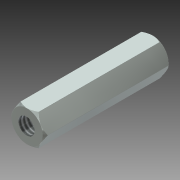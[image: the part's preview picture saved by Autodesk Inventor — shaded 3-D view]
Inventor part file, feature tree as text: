
AUTODESK INVENTOR PART (.ipt)
format: ipt  version: 2013 (Build 170138000, 138)  size: 134,144 bytes
history: native  units: mm (DEFAULTED — no unit token found)
features: sketch x4, plane x2, hole x2, extrude x1, revolve x1
ambient origin geometry x8: Origin, YZ Plane, XZ Plane, XY Plane, X Axis, Y Axis, Z Axis, Center Point
bodies: Solid1 (feature_tree)
feature tree (10):
  extrude  "Extrusion1"  Depth=25.4mm TaperAngle=0.0deg
  plane  "Work Plane1"
  revolve  "Revolution1"  [1 undecoded]
  hole  "Hole3"  [1 undecoded]
  hole  "Hole4"  [1 undecoded]
  plane  "Work Plane2"
  sketch  "Sketch1"  dims[d0=6.35mm d1=25.4mm d2=0.0mm]
  sketch  "Sketch3"  dims[d4=-3.175mm d5=0.508mm]
  sketch  "Sketch6"  dims[d6=0.508mm d7=0.508mm]
  sketch  "Sketch7"  dims[d8=0.508mm d16=0.0mm d17=90.0deg d32=3.302mm d33=12.7mm d34=9.525mm d35=6.35mm d36=14.3117mm d37=12.7mm d38=20.594885mm d39=3.302mm d40=19.05mm d41=9.525mm d42=6.35mm d43=14.3117mm d44=12.7mm d45=20.594885mm d46=0.508mm d47=0.508mm d48=0.508mm d49=0.508mm]
note: 3 required parameter values undecoded (feature->parameter linkage not recoverable at this tier; creation-order binding heuristic only, values carry confidence <= 0.55)